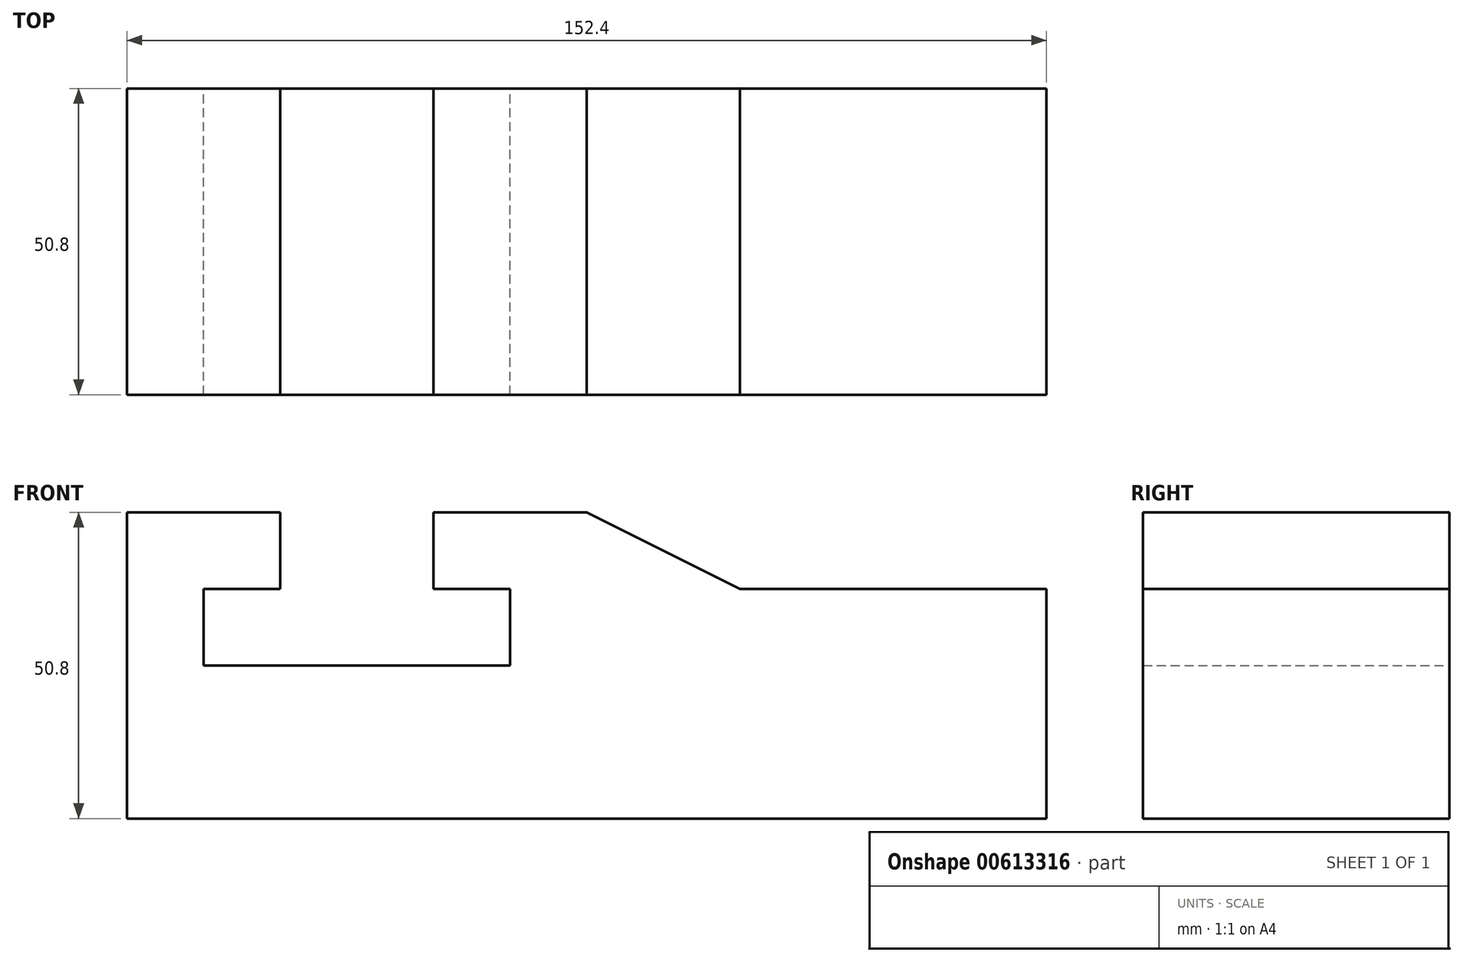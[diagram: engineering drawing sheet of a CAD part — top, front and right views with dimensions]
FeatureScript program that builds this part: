
annotation { "Feature Type Name" : "Feature", "Feature Type Description" : "" }
export const myFeature = defineFeature(function(context is Context, id is Id, definition is map)
    precondition{}
    {
        {
            var Q0;
            Q0=qCreatedBy(makeId("Front.planeOp"),FACE);
            var sketch = newSketch(context, id + "F0", { "sketchPlane" : qUnion([Q0])});
            skLineSegment(sketch, "E0", {"start": v(163.68, 0) * mm, "end": v(163.68, -50.8) * mm});
            skLineSegment(sketch, "E1", {"start": v(163.68, -50.8) * mm, "end": v(316.08, -50.8) * mm});
            skLineSegment(sketch, "E2", {"start": v(316.08, -50.8) * mm, "end": v(316.08, -12.7) * mm});
            skLineSegment(sketch, "E3", {"start": v(316.08, -12.7) * mm, "end": v(265.28, -12.7) * mm});
            skLineSegment(sketch, "E4", {"start": v(163.68, 0) * mm, "end": v(189.08, 0) * mm});
            skLineSegment(sketch, "E5", {"start": v(189.08, 0) * mm, "end": v(189.08, -12.7) * mm});
            skLineSegment(sketch, "E6", {"start": v(189.08, -12.7) * mm, "end": v(176.38, -12.7) * mm});
            skLineSegment(sketch, "E7", {"start": v(176.38, -12.7) * mm, "end": v(176.38, -25.4) * mm});
            skLineSegment(sketch, "E8", {"start": v(176.38, -25.4) * mm, "end": v(227.18, -25.4) * mm});
            skLineSegment(sketch, "E9", {"start": v(227.18, -25.4) * mm, "end": v(227.18, -12.7) * mm});
            skLineSegment(sketch, "E10", {"start": v(227.18, -12.7) * mm, "end": v(214.48, -12.7) * mm});
            skLineSegment(sketch, "E11", {"start": v(214.48, -12.7) * mm, "end": v(214.48, 0) * mm});
            skLineSegment(sketch, "E12", {"start": v(214.48, 0) * mm, "end": v(239.88, 0) * mm});
            skLineSegment(sketch, "E13", {"start": v(239.88, 0) * mm, "end": v(265.28, -12.7) * mm});
            skSolve(sketch);
        }
        {
            var Q0;
            Q0 = qSketchRegion(id + "F0", true);
            extrude(context, id + "F1", {"entities" : qUnion([Q0]), "depth" : 50.8 * mm, "offsetDistance" : 25.4 * mm});
        }
        {
            var Q0;
            Q0=qCreatedBy(makeId("Right.planeOp"),FACE);
            var sketch = newSketch(context, id + "F2", { "sketchPlane" : qUnion([Q0])});
            skLineSegment(sketch, "E14", {"start": v(-37.21, -49.91) * mm, "end": v(-11.81, -49.91) * mm});
            skLineSegment(sketch, "E15", {"start": v(-11.81, -49.91) * mm, "end": v(-7.24, -42.04) * mm});
            skLineSegment(sketch, "E16", {"start": v(-7.24, -42.04) * mm, "end": v(-42.8, -42.04) * mm});
            skLineSegment(sketch, "E17", {"start": v(-42.8, -42.04) * mm, "end": v(-37.21, -49.91) * mm});
            skSolve(sketch);
        }
        {
            var Q0;
            Q0 = qSketchRegion(id + "F2", true);
            extrude(context, id + "F3", {"entities" : qUnion([Q0]), "operationType" : NewBodyOperationType.REMOVE, "oppositeDirection" : true, "depth" : 254 * mm, "offsetDistance" : 25.4 * mm});
        }
    });
